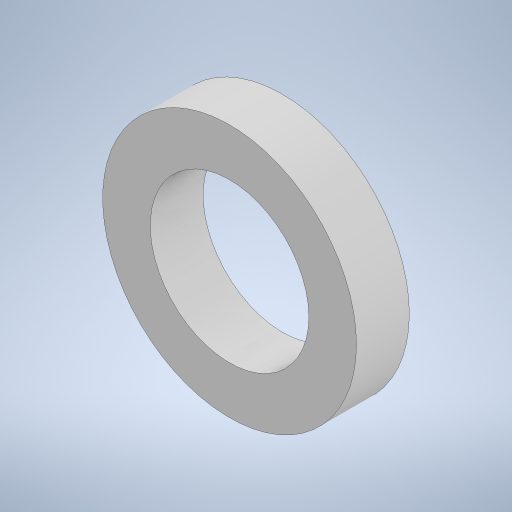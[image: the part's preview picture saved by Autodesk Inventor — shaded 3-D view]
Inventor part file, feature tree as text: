
AUTODESK INVENTOR PART (.ipt)
format: ipt  version: 2023 (Build 270158000, 158)  size: 223,232 bytes
history: native  units: in
note: dims shown in document units (in); Inventor stores cm internally (conversion verified against a paired STEP export)
features: extrude x1, sketch x1
ambient origin geometry x8: Origin, YZ Plane, XZ Plane, XY Plane, X Axis, Y Axis, Z Axis, Center Point
bodies: Solid1 (feature_tree)
feature tree (2):
  extrude  "Extrusion1"  Depth=0.1969in TaperAngle=0.0deg
  sketch  "Sketch1"  dims[d0=0.9449in d1=0.1969in d2=0.0in d3=0.5906in]
